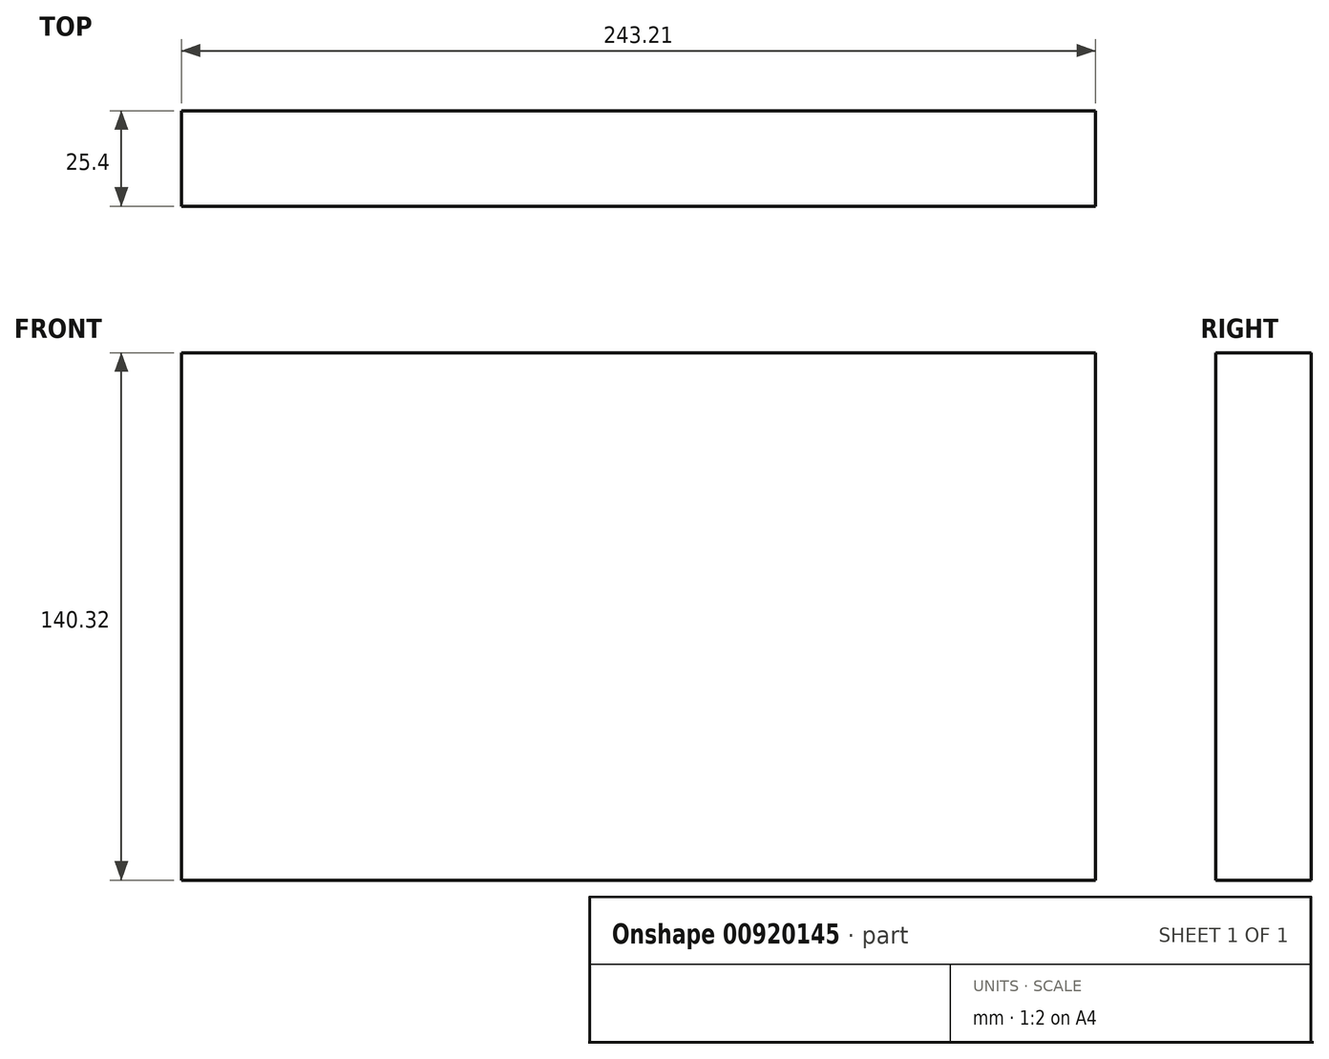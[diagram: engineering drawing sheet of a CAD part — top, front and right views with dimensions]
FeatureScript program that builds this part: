
annotation { "Feature Type Name" : "Feature", "Feature Type Description" : "" }
export const myFeature = defineFeature(function(context is Context, id is Id, definition is map)
    precondition{}
    {
        {
            var Q0;
            Q0=qCreatedBy(makeId("Front.planeOp"),FACE);
            var sketch = newSketch(context, id + "F0", { "sketchPlane" : qUnion([Q0])});
            skLineSegment(sketch, "E0.bottom", {"start": v(-128.53, 76.74) * mm, "end": v(114.68, 76.74) * mm});
            skLineSegment(sketch, "E0.top", {"start": v(-128.53, -63.58) * mm, "end": v(114.68, -63.58) * mm});
            skLineSegment(sketch, "E0.left", {"start": v(-128.53, 76.74) * mm, "end": v(-128.53, -63.58) * mm});
            skLineSegment(sketch, "E0.right", {"start": v(114.68, 76.74) * mm, "end": v(114.68, -63.58) * mm});
            skSolve(sketch);
        }
        {
            var Q0;
            Q0=makeQuery(id+"F0.imprint","IMPRINT",FACE,{"disambiguationData":[TD([[makeQuery(id+"F0.imprint","IMPRINT",EDGE,{"derivedFrom":sQuery(id+"F0.wireOp",EDGE,"E0.bottom")}),-1.0]])]});
            extrude(context, id + "F1", {"entities" : qUnion([Q0]), "depth" : 25.4 * mm, "offsetDistance" : 25.4 * mm});
        }
    });
